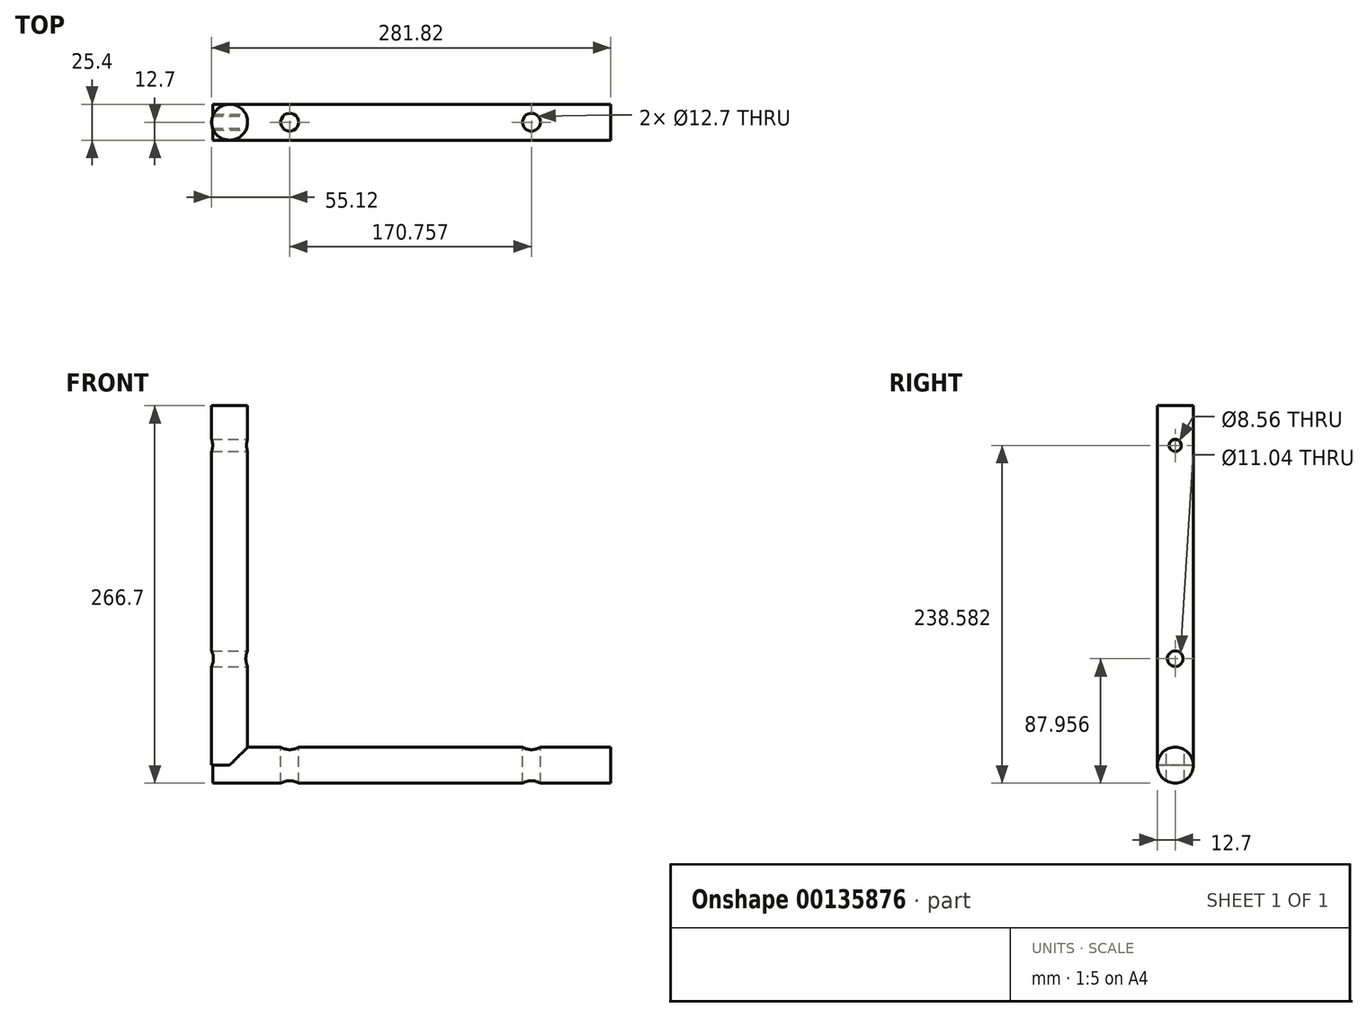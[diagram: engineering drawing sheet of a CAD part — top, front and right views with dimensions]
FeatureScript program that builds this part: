
annotation { "Feature Type Name" : "Feature", "Feature Type Description" : "" }
export const myFeature = defineFeature(function(context is Context, id is Id, definition is map)
    precondition{}
    {
        {
            var Q0;
            Q0=qCreatedBy(makeId("Top.planeOp"),FACE);
            var sketch = newSketch(context, id + "F0", { "sketchPlane" : qUnion([Q0])});
            skCircle(sketch, "E0", {"center": v(0, 0) * mm, "radius": 12.7 * mm});
            skSolve(sketch);
        }
        {
            var Q0;
            Q0 = qSketchRegion(id + "F0", true);
            extrude(context, id + "F1", {"entities" : qUnion([Q0]), "depth" : 254 * mm});
        }
        {
            var Q0;
            Q0=qCreatedBy(makeId("Right.planeOp"),FACE);
            var sketch = newSketch(context, id + "F2", { "sketchPlane" : qUnion([Q0])});
            skCircle(sketch, "E1", {"center": v(0, 0) * mm, "radius": 12.7 * mm});
            skSolve(sketch);
        }
        {
            var Q0;
            Q0=makeQuery(id+"F2.imprint","IMPRINT",FACE,{"disambiguationData":[TD([[makeQuery(id+"F2.imprint","IMPRINT",EDGE,{"derivedFrom":sQuery(id+"F2.wireOp",EDGE,"E1")}),1.0]])]});
            extrude(context, id + "F3", {"entities" : qUnion([Q0]), "operationType" : NewBodyOperationType.ADD, "endBound" : BoundingType.THROUGH_ALL, "depth" : 254 * mm});
        }
        {
            var Q0;
            Q0=makeQuery(id+"F3.opExtrude","CAP_FACE",FACE,{"disambiguationData":[OSD([sQuery(id+"F2.wireOp",EDGE,"E1")])],"isStart":true});
            var sketch = newSketch(context, id + "F4", { "sketchPlane" : qUnion([Q0])});
            skSolve(sketch);
        }
        {
            var Q0;
            {var subQ0=sQuery(id+"F2.wireOp",EDGE,"E1");Q0=makeQuery(id+"F4.imprint","IMPRINT",FACE,{"disambiguationData":[TD([[makeQuery(id+"F4.imprint","IMPRINT",EDGE,{"derivedFrom":makeQuery(id+"F3.opExtrude","CAP_EDGE",EDGE,{"disambiguationData":[OSD([subQ0])],"isStart":true})}),-1.0]])]});}
            extrude(context, id + "F5", {"entities" : qUnion([Q0]), "operationType" : NewBodyOperationType.ADD, "depth" : 12 * mm});
        }
        {
            var Q0;
            Q0=qCreatedBy(makeId("Right.planeOp"),FACE);
            var sketch = newSketch(context, id + "F6", { "sketchPlane" : qUnion([Q0])});
            skCircle(sketch, "E2", {"center": v(0, 225.88) * mm, "radius": 4.28 * mm});
            skSolve(sketch);
        }
        {
            var Q0;
            Q0 = qSketchRegion(id + "F6", true);
            extrude(context, id + "F7", {"entities" : qUnion([Q0]), "operationType" : NewBodyOperationType.REMOVE, "oppositeDirection" : true, "depth" : 25.4 * mm, "symmetric" : true});
        }
        {
            var Q0;
            Q0=qCreatedBy(makeId("Right.planeOp"),FACE);
            var sketch = newSketch(context, id + "F8", { "sketchPlane" : qUnion([Q0])});
            skCircle(sketch, "E3", {"center": v(0, 75.26) * mm, "radius": 5.52 * mm});
            skSolve(sketch);
        }
        {
            var Q0;
            Q0 = qSketchRegion(id + "F8", true);
            extrude(context, id + "F9", {"entities" : qUnion([Q0]), "operationType" : NewBodyOperationType.REMOVE, "oppositeDirection" : true, "depth" : 25.4 * mm, "symmetric" : true});
        }
        {
            var Q0;
            Q0=qCreatedBy(makeId("Top.planeOp"),FACE);
            var sketch = newSketch(context, id + "F10", { "sketchPlane" : qUnion([Q0])});
            skCircle(sketch, "E4", {"center": v(42.42, 0) * mm, "radius": 6.35 * mm});
            skCircle(sketch, "E5", {"center": v(213.18, 0) * mm, "radius": 6.35 * mm});
            skSolve(sketch);
        }
        {
            var Q0;
            Q0 = qSketchRegion(id + "F10", true);
            extrude(context, id + "F11", {"entities" : qUnion([Q0]), "operationType" : NewBodyOperationType.REMOVE, "oppositeDirection" : true, "depth" : 25.4 * mm, "symmetric" : true});
        }
    });
